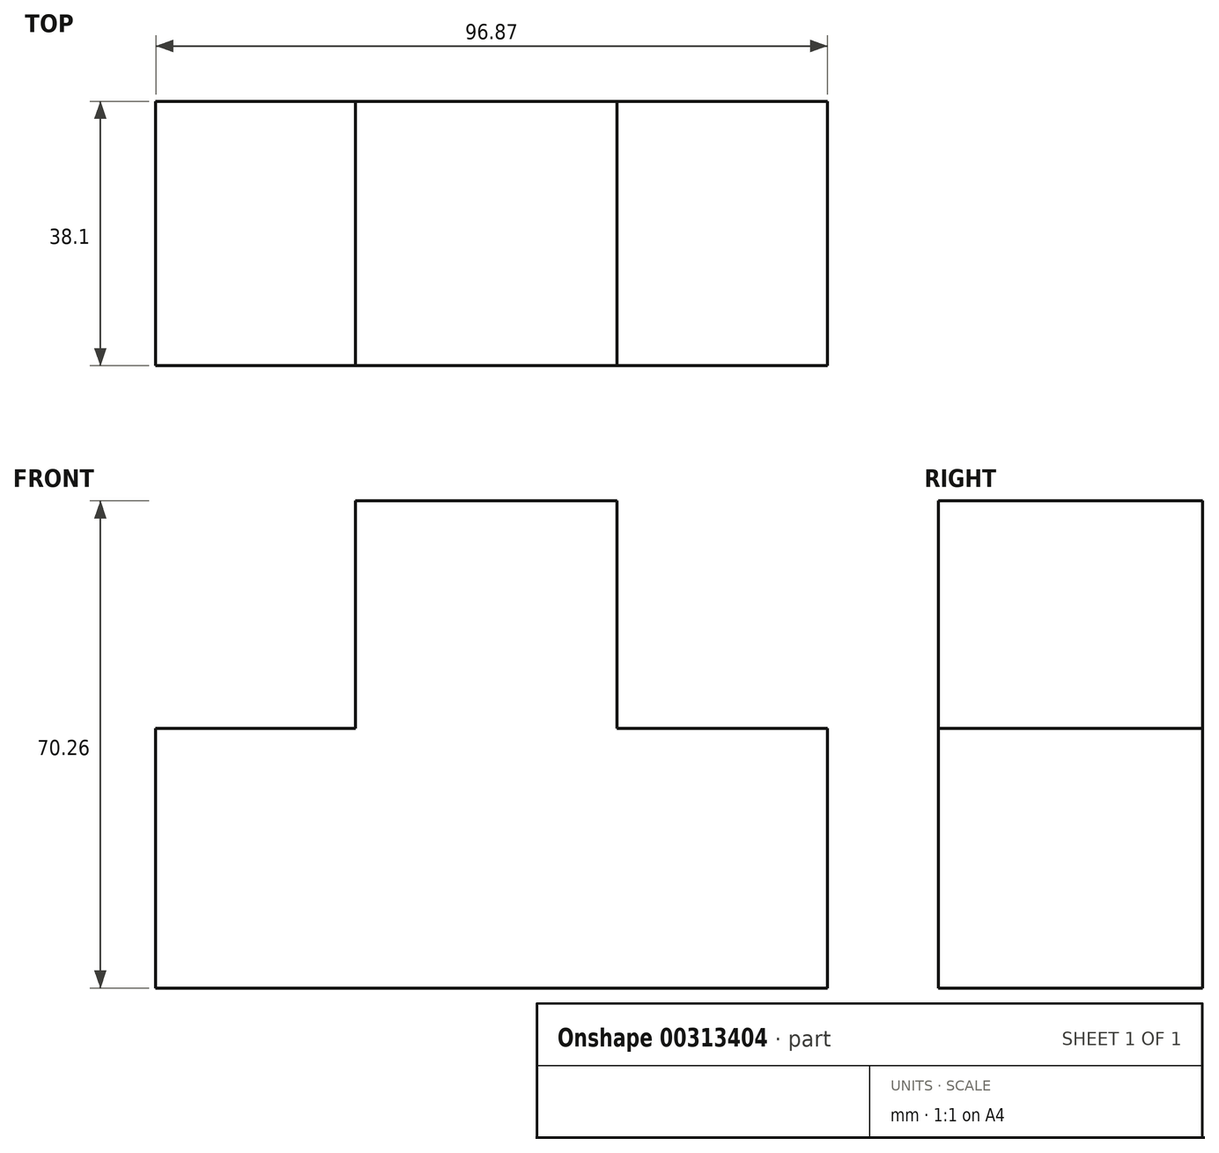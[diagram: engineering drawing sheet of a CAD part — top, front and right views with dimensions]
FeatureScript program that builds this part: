
annotation { "Feature Type Name" : "Feature", "Feature Type Description" : "" }
export const myFeature = defineFeature(function(context is Context, id is Id, definition is map)
    precondition{}
    {
        {
            var Q0;
            Q0=qCreatedBy(makeId("Front.planeOp"),FACE);
            var sketch = newSketch(context, id + "F0", { "sketchPlane" : qUnion([Q0])});
            skLineSegment(sketch, "E0", {"start": v(-48.6, -49.06) * mm, "end": v(48.28, -49.06) * mm});
            skLineSegment(sketch, "E1", {"start": v(48.28, -49.06) * mm, "end": v(48.28, -11.6) * mm});
            skLineSegment(sketch, "E2", {"start": v(48.28, -11.6) * mm, "end": v(17.95, -11.6) * mm});
            skLineSegment(sketch, "E3", {"start": v(17.95, -11.6) * mm, "end": v(17.95, 21.2) * mm});
            skLineSegment(sketch, "E4", {"start": v(17.95, 21.2) * mm, "end": v(-19.8, 21.2) * mm});
            skLineSegment(sketch, "E5", {"start": v(-19.8, 21.2) * mm, "end": v(-19.8, -11.6) * mm});
            skLineSegment(sketch, "E6", {"start": v(-19.8, -11.6) * mm, "end": v(-48.6, -11.6) * mm});
            skLineSegment(sketch, "E7", {"start": v(-48.6, -11.6) * mm, "end": v(-48.6, -49.06) * mm});
            skSolve(sketch);
        }
        {
            var Q0;
            Q0 = qSketchRegion(id + "F0", true);
            extrude(context, id + "F1", {"entities" : qUnion([Q0]), "depth" : 38.1 * mm});
        }
    });
